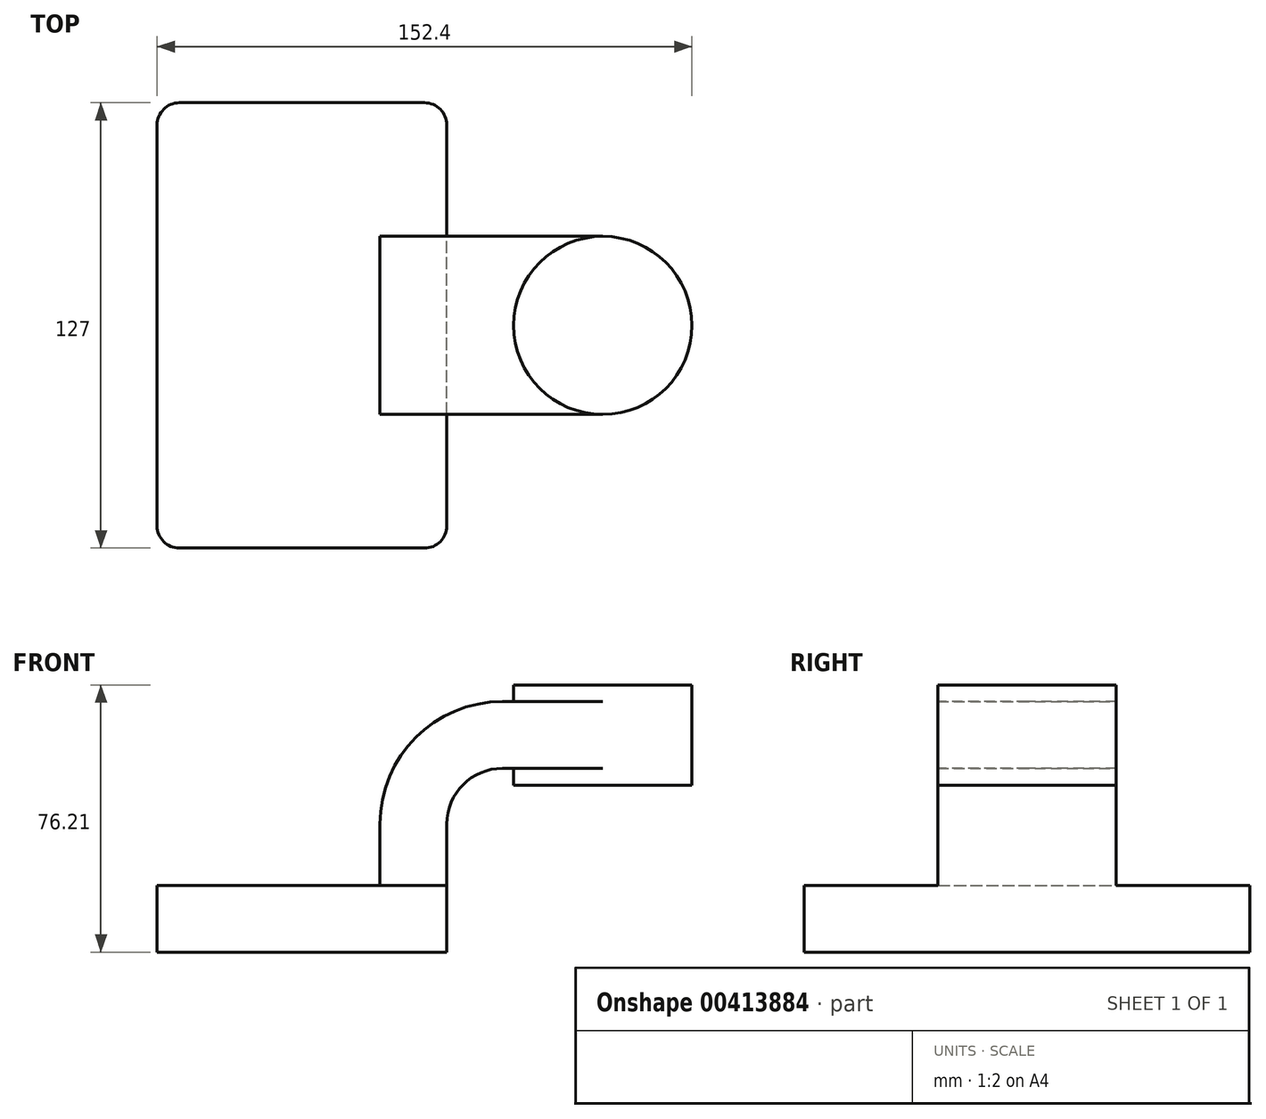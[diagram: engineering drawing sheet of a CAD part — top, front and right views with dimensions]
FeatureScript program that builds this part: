
annotation { "Feature Type Name" : "Feature", "Feature Type Description" : "" }
export const myFeature = defineFeature(function(context is Context, id is Id, definition is map)
    precondition{}
    {
        {
            var Q0;
            Q0=qCreatedBy(makeId("Front.planeOp"),FACE);
            var sketch = newSketch(context, id + "F0", { "sketchPlane" : qUnion([Q0])});
            skLineSegment(sketch, "E0.bottom", {"start": v(-41.28, 9.52) * mm, "end": v(41.27, 9.53) * mm});
            skLineSegment(sketch, "E0.top", {"start": v(-41.28, -9.52) * mm, "end": v(41.28, -9.52) * mm});
            skLineSegment(sketch, "E0.left", {"start": v(-41.28, 9.52) * mm, "end": v(-41.28, -9.53) * mm});
            skLineSegment(sketch, "E0.right", {"start": v(41.27, 9.53) * mm, "end": v(41.28, -9.52) * mm});
            skPoint(sketch, "E0.middle", {"position": v(0, 0) * mm});
            skLineSegment(sketch, "E1.bottom", {"start": v(60.32, 66.68) * mm, "end": v(111.12, 66.68) * mm});
            skLineSegment(sketch, "E1.top", {"start": v(60.32, 38.1) * mm, "end": v(111.12, 38.1) * mm});
            skLineSegment(sketch, "E1.left", {"start": v(60.32, 66.68) * mm, "end": v(60.32, 38.1) * mm});
            skLineSegment(sketch, "E1.right", {"start": v(111.12, 66.68) * mm, "end": v(111.12, 38.1) * mm});
            skPoint(sketch, "E1.middle", {"position": v(85.72, 52.39) * mm});
            skLineSegment(sketch, "E2", {"start": v(41.27, 9.53) * mm, "end": v(41.27, 27) * mm});
            skArc(sketch, "E3", {"start": v(41.27, 27) * mm, "mid": v(45.92, 38.23) * mm, "end": v(57.15, 42.88) * mm});
            skPoint(sketch, "E4.endSnap0", {"position": v(85.72, 38.1) * mm});
            skLineSegment(sketch, "E5", {"start": v(57.15, 42.88) * mm, "end": v(85.72, 42.88) * mm});
            skLineSegment(sketch, "E6.0", {"start": v(57.15, 61.93) * mm, "end": v(85.72, 61.93) * mm});
            skArc(sketch, "E6.1", {"start": v(22.22, 27) * mm, "mid": v(32.45, 51.7) * mm, "end": v(57.15, 61.93) * mm});
            skLineSegment(sketch, "E6.2", {"start": v(22.22, 9.53) * mm, "end": v(22.22, 27) * mm});
            skLineSegment(sketch, "E7", {"start": v(85.72, 38.1) * mm, "end": v(85.72, 66.68) * mm});
            skFitSpline(sketch, "E8", {"points": [v(-41.28, 9.53) * mm, v(57.15, 61.93) * mm], "startDerivative": vector(50.05, 95.2) * mm, "endDerivative": vector(144.32, -27) * mm});
            skSolve(sketch);
        }
        {
            var Q0;
            Q0=makeQuery(id+"F0.imprint","IMPRINT",FACE,{"disambiguationData":[TD([[makeQuery(id+"F0.imprint","IMPRINT",EDGE,{"derivedFrom":sQuery(id+"F0.wireOp",EDGE,"E0.top")}),1.0]])]});
            extrude(context, id + "F1", {"entities" : qUnion([Q0]), "endBound" : BoundingType.SYMMETRIC, "depth" : 127 * mm});
        }
        {
            var Q0;
            {var subQ1=sQuery(id+"F0.wireOp",EDGE,"E2");Q0=makeQuery(id+"F0.imprint","IMPRINT",FACE,{"disambiguationData":[TD([[makeQuery(id+"F0.imprint","IMPRINT",EDGE,{"derivedFrom":subQ1}),1.0]])]});}
            var Q1;
            {var subQ0=sQuery(id+"F0.wireOp",EDGE,"E6.0");var subQ1=sQuery(id+"F0.wireOp",EDGE,"E1.left");var subQ2=makeQuery(id+"F0.imprint","INTERSECT",VERTEX,{"derivedFrom":[subQ1,subQ0]});Q1=makeQuery(id+"F0.imprint","IMPRINT",FACE,{"disambiguationData":[TD([[makeQuery(id+"F0.imprint","IMPRINT",EDGE,{"disambiguationData":[TD([[subQ2,-1.0]])],"derivedFrom":subQ1}),1.0]])]});}
            extrude(context, id + "F2", {"entities" : qUnion([Q0, Q1]), "operationType" : NewBodyOperationType.ADD, "endBound" : BoundingType.SYMMETRIC, "depth" : 50.8 * mm});
        }
        {
            var Q0;
            Q0=makeQuery(id+"F0.imprint","IMPRINT",FACE,{"disambiguationData":[TD([[makeQuery(id+"F0.imprint","IMPRINT",EDGE,{"derivedFrom":sQuery(id+"F0.wireOp",EDGE,"E6.1")}),1.0]])]});
            extrude(context, id + "F3", {"entities" : qUnion([Q0]), "operationType" : NewBodyOperationType.ADD, "endBound" : BoundingType.SYMMETRIC, "depth" : 15.88 * mm});
        }
        {
            var Q0;
            {var subQ0=sQuery(id+"F0.wireOp",EDGE,"E1.right");Q0=makeQuery(id+"F0.imprint","IMPRINT",FACE,{"disambiguationData":[TD([[makeQuery(id+"F0.imprint","IMPRINT",EDGE,{"derivedFrom":subQ0}),-1.0]])]});}
            var Q1;
            Q1=sQuery(id+"F0.wireOp",EDGE,"E7");
            revolve(context, id + "F4", {"operationType" : NewBodyOperationType.ADD, "entities" : qUnion([Q0]), "axis" : qUnion([Q1]), "revolveType" : RevolveType.FULL});
        }
        {
            var Q0;
            Q0=makeQuery(id+"F1.opExtrude","CAP_EDGE",EDGE,{"disambiguationData":[OSD([sQuery(id+"F0.wireOp",EDGE,"E0.left")])],"isStart":false});
            var Q1;
            Q1=makeQuery(id+"F1.opExtrude","CAP_EDGE",EDGE,{"disambiguationData":[OSD([sQuery(id+"F0.wireOp",EDGE,"E0.right")])],"isStart":false});
            var Q2;
            Q2=makeQuery(id+"F1.opExtrude","CAP_EDGE",EDGE,{"disambiguationData":[OSD([sQuery(id+"F0.wireOp",EDGE,"E0.right")])],"isStart":true});
            var Q3;
            Q3=makeQuery(id+"F1.opExtrude","CAP_EDGE",EDGE,{"disambiguationData":[OSD([sQuery(id+"F0.wireOp",EDGE,"E0.left")])],"isStart":true});
            fillet(context, id + "F5", {"entities" : qUnion([Q0, Q1, Q2, Q3]), "radius" : 6.35 * mm, "tangentPropagation" : true, "allowEdgeOverflow" : false});
        }
    });
